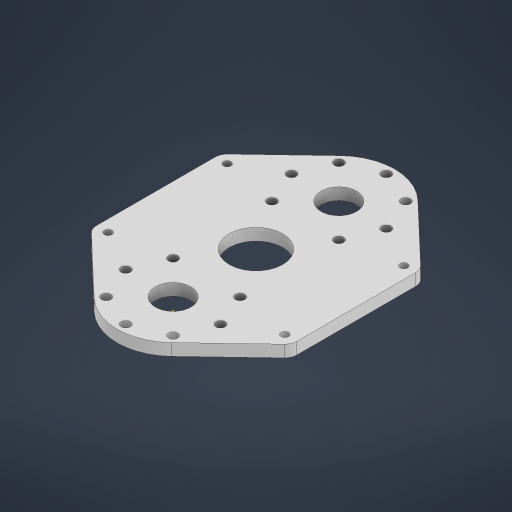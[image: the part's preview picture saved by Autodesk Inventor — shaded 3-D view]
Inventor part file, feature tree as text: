
AUTODESK INVENTOR PART (.ipt)
format: ipt  version: 2024.3 (Build 283343000, 343)  size: 244,224 bytes
history: native  units: in
note: dims shown in document units (in); Inventor stores cm internally (conversion verified against a paired STEP export)
features: sketch x2, extrude x1
ambient origin geometry x8: Origin, YZ Plane, XZ Plane, XY Plane, X Axis, Y Axis, Z Axis, Center Point
bodies: Solid1 (feature_tree)
feature tree (3):
  sketch  "Sketch1"  dims[d0=0.5in d1=3.0in]
  extrude  "Extrusion1"  Depth=3.0in
  sketch  "Sketch2"  dims[d2=2.0in d3=0.196in d4=3.1496in d6=360.0deg d8=0.196in d9=3.1496in d11=360.0deg d13=0.75in d14=0.75in d15=2.36in d16=2.36in d17=0.5in d18=0.159in d24=0.5in d25=1.13in d26=0.25in d27=0.125in d28=0.0in d29=0.0in]
